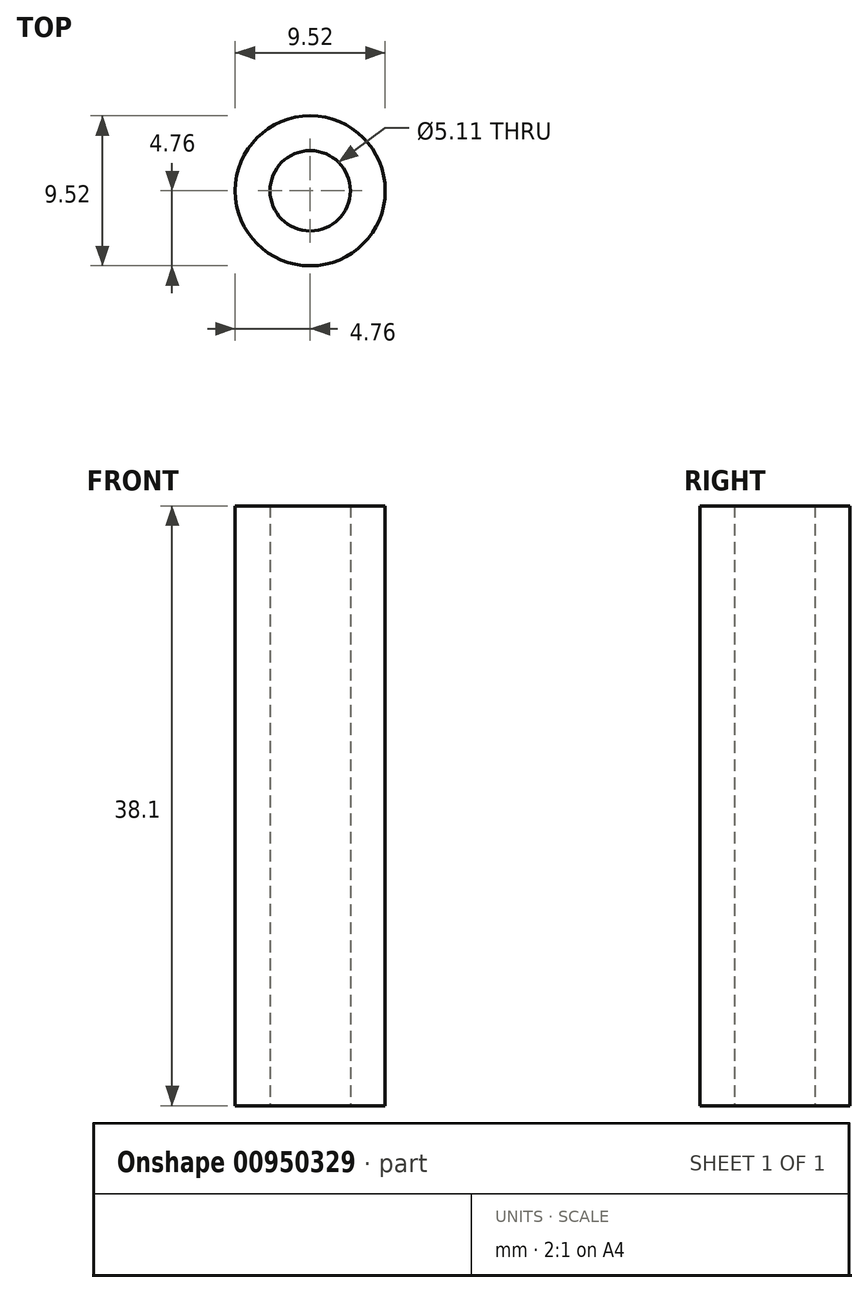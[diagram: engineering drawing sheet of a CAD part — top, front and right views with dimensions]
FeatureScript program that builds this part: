
annotation { "Feature Type Name" : "Feature", "Feature Type Description" : "" }
export const myFeature = defineFeature(function(context is Context, id is Id, definition is map)
    precondition{}
    {
        {
            var Q0;
            Q0=qCreatedBy(makeId("Top.planeOp"),FACE);
            var sketch = newSketch(context, id + "F0", { "sketchPlane" : qUnion([Q0])});
            skCircle(sketch, "E0", {"center": v(0, 0) * mm, "radius": 2.55 * mm});
            skCircle(sketch, "E1", {"center": v(0, 0) * mm, "radius": 4.76 * mm});
            skSolve(sketch);
        }
        {
            var Q0;
            Q0=makeQuery(id+"F0.imprint","IMPRINT",FACE,{"disambiguationData":[TD([[makeQuery(id+"F0.imprint","IMPRINT",EDGE,{"derivedFrom":sQuery(id+"F0.wireOp",EDGE,"E0")}),-1.0]])]});
            extrude(context, id + "F1", {"entities" : qUnion([Q0]), "depth" : 38.1 * mm, "offsetDistance" : 25.4 * mm});
        }
    });
